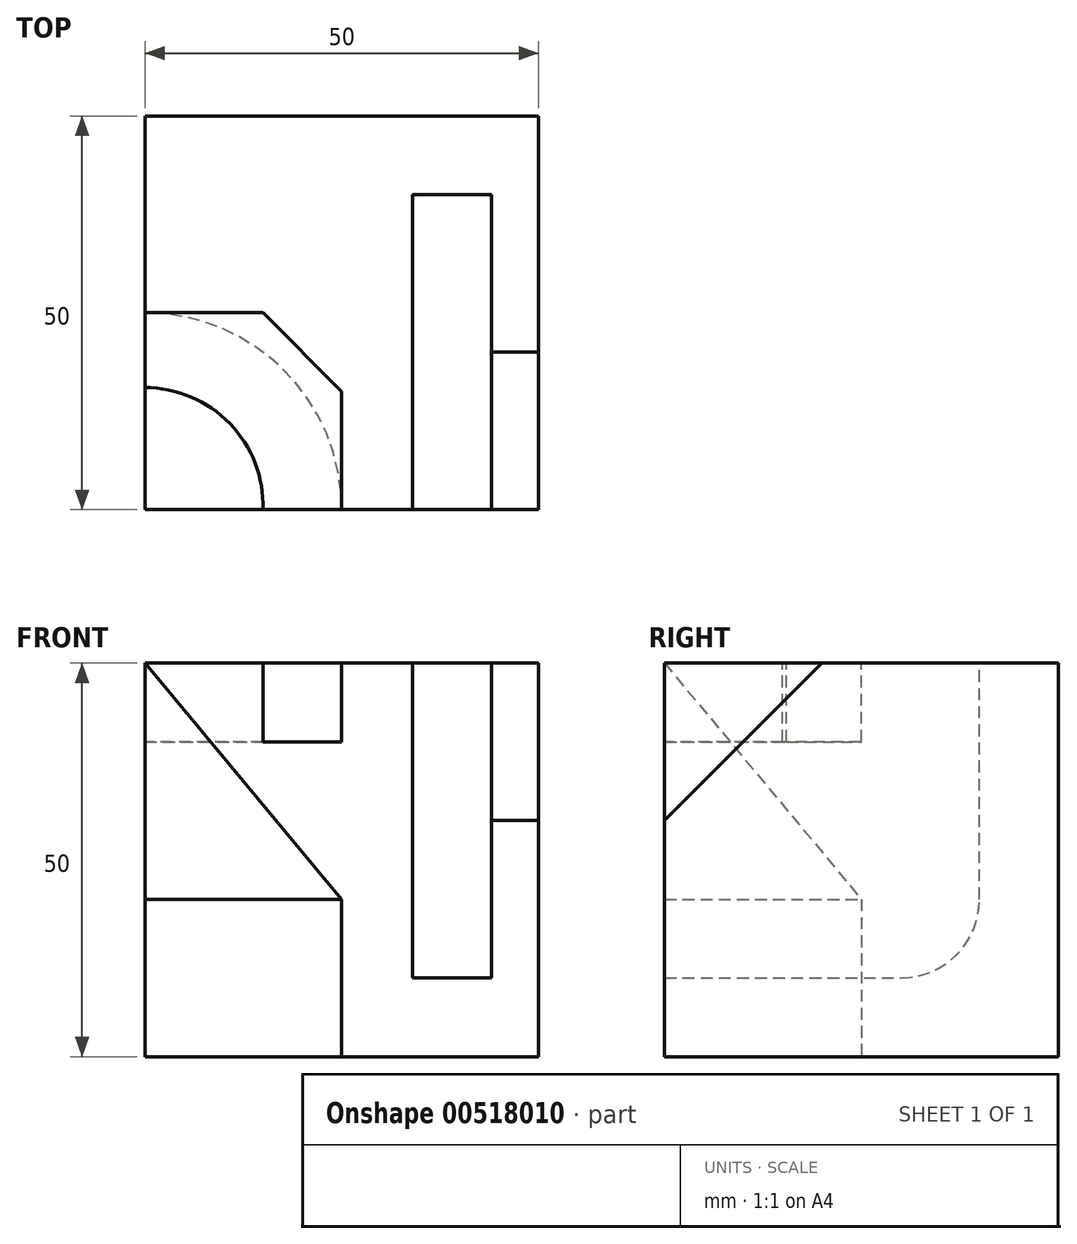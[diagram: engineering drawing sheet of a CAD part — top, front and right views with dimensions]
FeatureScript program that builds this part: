
annotation { "Feature Type Name" : "Feature", "Feature Type Description" : "" }
export const myFeature = defineFeature(function(context is Context, id is Id, definition is map)
    precondition{}
    {
        {
            var Q0;
            Q0=qCreatedBy(makeId("Front.planeOp"),FACE);
            var sketch = newSketch(context, id + "F0", { "sketchPlane" : qUnion([Q0])});
            skLineSegment(sketch, "E0.bottom", {"start": v(0, 0) * mm, "end": v(50, 0) * mm});
            skLineSegment(sketch, "E0.top", {"start": v(0, 50) * mm, "end": v(50, 50) * mm});
            skLineSegment(sketch, "E0.left", {"start": v(0, 0) * mm, "end": v(0, 50) * mm});
            skLineSegment(sketch, "E0.right", {"start": v(50, 0) * mm, "end": v(50, 50) * mm});
            skSolve(sketch);
        }
        {
            var Q0;
            Q0 = qSketchRegion(id + "F0", true);
            extrude(context, id + "F1", {"entities" : qUnion([Q0]), "depth" : 50 * mm, "offsetDistance" : 25 * mm});
        }
        {
            var Q0;
            Q0=makeQuery(id+"F1.opExtrude","SWEPT_FACE",FACE,{"disambiguationData":[OSD([sQuery(id+"F0.wireOp",EDGE,"E0.top")])]});
            var sketch = newSketch(context, id + "F2", { "sketchPlane" : qUnion([Q0])});
            skLineSegment(sketch, "E1.bottom", {"start": v(34, -50) * mm, "end": v(44, -50) * mm});
            skLineSegment(sketch, "E1.top", {"start": v(34, -10) * mm, "end": v(44, -10) * mm});
            skLineSegment(sketch, "E1.left", {"start": v(34, -50) * mm, "end": v(34, -10) * mm});
            skLineSegment(sketch, "E1.right", {"start": v(44, -50) * mm, "end": v(44, -10) * mm});
            skSolve(sketch);
        }
        {
            var Q0;
            Q0 = qSketchRegion(id + "F2", true);
            extrude(context, id + "F3", {"entities" : qUnion([Q0]), "operationType" : NewBodyOperationType.REMOVE, "oppositeDirection" : true, "depth" : 40 * mm, "offsetDistance" : 25 * mm});
        }
        {
            var Q0;
            Q0=makeQuery(id+"F3.boolean.opBoolean","COPY",EDGE,{"derivedFrom":makeQuery(id+"F3.opExtrude","CAP_EDGE",EDGE,{"disambiguationData":[OSD([sQuery(id+"F2.wireOp",EDGE,"E1.top")])],"isStart":false})});
            fillet(context, id + "F4", {"entities" : qUnion([Q0]), "radius" : 10 * mm, "tangentPropagation" : true, "allowEdgeOverflow" : false});
        }
        {
            var Q0;
            {var subQ0=sQuery(id+"F0.wireOp",EDGE,"E0.right");var subQ1=sQuery(id+"F0.wireOp",EDGE,"E0.top");Q0=makeQuery(id+"F3.boolean.opBoolean","SPLIT",EDGE,{"disambiguationData":[TD([makeQuery(id+"F1.opExtrude","SWEPT_FACE",FACE,{"disambiguationData":[OSD([subQ0])]})])],"derivedFrom":makeQuery(id+"F1.opExtrude","CAP_EDGE",EDGE,{"disambiguationData":[OSD([subQ1])],"isStart":false})});}
            chamfer(context, id + "F5", {"entities" : qUnion([Q0]), "width" : 20 * mm, "tangentPropagation" : true});
        }
        {
            var Q0;
            Q0=makeQuery(id+"F1.opExtrude","CAP_FACE",FACE,{"disambiguationData":[OSD([sQuery(id+"F0.wireOp",EDGE,"E0.bottom"),sQuery(id+"F0.wireOp",EDGE,"E0.top"),sQuery(id+"F0.wireOp",EDGE,"E0.left"),sQuery(id+"F0.wireOp",EDGE,"E0.right")])],"isStart":false});
            var sketch = newSketch(context, id + "F6", { "sketchPlane" : qUnion([Q0])});
            skLineSegment(sketch, "E2", {"start": v(0, 50) * mm, "end": v(25, 20) * mm});
            skLineSegment(sketch, "E3", {"start": v(25, 20) * mm, "end": v(25, 0) * mm});
            skSolve(sketch);
        }
        {
            var Q0;
            Q0=makeQuery(id+"F6.imprint","IMPRINT",FACE,{"disambiguationData":[TD([[makeQuery(id+"F6.imprint","IMPRINT",EDGE,{"derivedFrom":sQuery(id+"F6.wireOp",EDGE,"E2")}),-1.0]])]});
            var Q1;
            Q1=makeQuery(id+"F1.opExtrude","CAP_EDGE",EDGE,{"disambiguationData":[OSD([sQuery(id+"F0.wireOp",EDGE,"E0.left")])],"isStart":false});
            revolve(context, id + "F7", {"operationType" : NewBodyOperationType.REMOVE, "entities" : qUnion([Q0]), "axis" : qUnion([Q1]), "revolveType" : RevolveType.SYMMETRIC, "oppositeDirection" : true, "angle" : 180 * degree});
        }
        {
            var Q0;
            Q0=makeQuery(id+"F1.opExtrude","SWEPT_FACE",FACE,{"disambiguationData":[OSD([sQuery(id+"F0.wireOp",EDGE,"E0.top")])]});
            var sketch = newSketch(context, id + "F8", { "sketchPlane" : qUnion([Q0])});
            skLineSegment(sketch, "E4", {"start": v(0, -25) * mm, "end": v(15, -25) * mm});
            skLineSegment(sketch, "E5", {"start": v(15, -25) * mm, "end": v(25, -35) * mm});
            skLineSegment(sketch, "E6", {"start": v(25, -35) * mm, "end": v(25, -50) * mm});
            skSolve(sketch);
        }
        {
            var Q0;
            {var subQ6=sQuery(id+"F8.wireOp",EDGE,"E4");Q0=makeQuery(id+"F8.imprint","IMPRINT",FACE,{"disambiguationData":[TD([[makeQuery(id+"F8.imprint","IMPRINT",EDGE,{"derivedFrom":subQ6}),-1.0]])]});}
            var sketch = newSketch(context, id + "F9", { "sketchPlane" : qUnion([Q0])});
            skCircle(sketch, "E7", {"center": v(0, -49.5) * mm, "radius": 15 * mm});
            skSolve(sketch);
        }
        {
            var Q0;
            {var subQ2=sQuery(id+"F8.wireOp",EDGE,"E4");var subQ3=makeQuery(id+"F8.imprint","IMPRINT",EDGE,{"derivedFrom":subQ2});Q0=makeQuery(id+"F9.imprint","IMPRINT",FACE,{"disambiguationData":[TD([[makeQuery(id+"F9.imprint","IMPRINT",EDGE,{"derivedFrom":subQ3}),-1.0]])]});}
            extrude(context, id + "F10", {"entities" : qUnion([Q0]), "operationType" : NewBodyOperationType.REMOVE, "oppositeDirection" : true, "depth" : 10 * mm, "offsetDistance" : 25 * mm});
        }
    });
